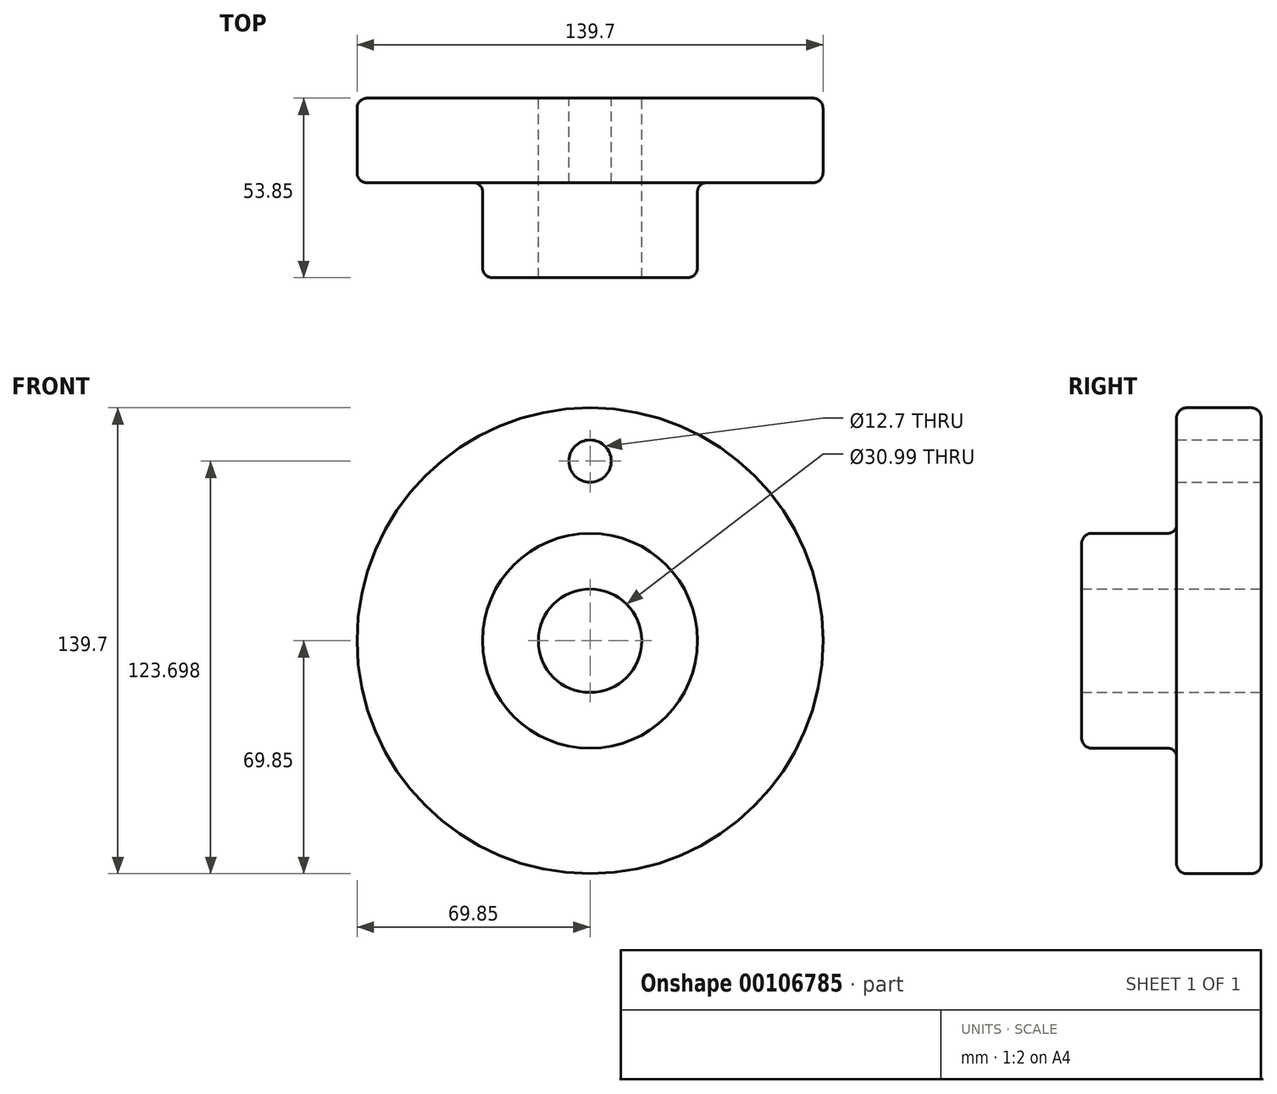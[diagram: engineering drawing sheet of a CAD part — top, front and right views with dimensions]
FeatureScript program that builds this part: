
annotation { "Feature Type Name" : "Feature", "Feature Type Description" : "" }
export const myFeature = defineFeature(function(context is Context, id is Id, definition is map)
    precondition{}
    {
        {
            var Q0;
            Q0=qCreatedBy(makeId("Front.planeOp"),FACE);
            var sketch = newSketch(context, id + "F0", { "sketchPlane" : qUnion([Q0])});
            skCircle(sketch, "E0", {"center": v(0, 0) * mm, "radius": 69.85 * mm});
            skSolve(sketch);
        }
        {
            var Q0;
            Q0 = qSketchRegion(id + "F0", true);
            extrude(context, id + "F1", {"entities" : qUnion([Q0]), "depth" : 25.4 * mm});
        }
        {
            var Q0;
            Q0=qCreatedBy(makeId("Front.planeOp"),FACE);
            var sketch = newSketch(context, id + "F2", { "sketchPlane" : qUnion([Q0])});
            skCircle(sketch, "E1", {"center": v(0, 0) * mm, "radius": 19.05 * mm});
            skCircle(sketch, "E2", {"center": v(0, 53.85) * mm, "radius": 6.35 * mm});
            skCircle(sketch, "E3", {"center": v(0, 0) * mm, "radius": 53.85 * mm, "construction": true});
            skSolve(sketch);
        }
        {
            var Q0;
            Q0 = qSketchRegion(id + "F2", true);
            extrude(context, id + "F3", {"entities" : qUnion([Q0]), "operationType" : NewBodyOperationType.REMOVE, "endBound" : BoundingType.THROUGH_ALL, "depth" : 25.4 * mm});
        }
        {
            var Q0;
            Q0=qCreatedBy(makeId("Right.planeOp"),FACE);
            var sketch = newSketch(context, id + "F4", { "sketchPlane" : qUnion([Q0])});
            skLineSegment(sketch, "E4", {"start": v(0, 0) * mm, "end": v(-45.3, 0) * mm, "construction": true});
            skLineSegment(sketch, "E5.bottom", {"start": v(0, 15.5) * mm, "end": v(-53.85, 15.5) * mm});
            skLineSegment(sketch, "E5.top", {"start": v(0, 32.23) * mm, "end": v(-50.8, 32.23) * mm});
            skLineSegment(sketch, "E5.left", {"start": v(0, 15.5) * mm, "end": v(0, 32.23) * mm});
            skLineSegment(sketch, "E5.right", {"start": v(-53.85, 15.5) * mm, "end": v(-53.85, 29.18) * mm});
            skPoint(sketch, "E6.visualSharp", {"position": v(-53.85, 32.23) * mm});
            skArc(sketch, "E6.filletArc", {"start": v(-50.8, 32.23) * mm, "mid": v(-52.96, 31.34) * mm, "end": v(-53.85, 29.18) * mm});
            skLineSegment(sketch, "E7.bottom", {"start": v(0, 32.23) * mm, "end": v(-25.3, 32.23) * mm});
            skLineSegment(sketch, "E7.top", {"start": v(0, 70) * mm, "end": v(-25.3, 70) * mm});
            skLineSegment(sketch, "E7.left", {"start": v(0, 32.23) * mm, "end": v(0, 70) * mm});
            skLineSegment(sketch, "E7.right", {"start": v(-25.3, 32.23) * mm, "end": v(-25.3, 70) * mm});
            skSolve(sketch);
        }
        {
            var Q0;
            Q0=makeQuery(id+"F4.imprint","IMPRINT",FACE,{"disambiguationData":[TD([[makeQuery(id+"F4.imprint","IMPRINT",EDGE,{"derivedFrom":sQuery(id+"F4.wireOp",EDGE,"E5.bottom")}),-1.0]])]});
            var Q1;
            Q1=sQuery(id+"F4.wireOp",EDGE,"E4");
            revolve(context, id + "F5", {"operationType" : NewBodyOperationType.ADD, "entities" : qUnion([Q0]), "axis" : qUnion([Q1]), "revolveType" : RevolveType.FULL});
        }
        {
            var Q0;
            Q0=makeQuery(id+"F1.opExtrude","CAP_EDGE",EDGE,{"disambiguationData":[OSD([sQuery(id+"F0.wireOp",EDGE,"E0")])],"isStart":false});
            fillet(context, id + "F6", {"entities" : qUnion([Q0]), "radius" : 3.05 * mm, "tangentPropagation" : true, "allowEdgeOverflow" : false});
        }
        {
            var Q0;
            Q0=makeQuery(id+"F1.opExtrude","CAP_EDGE",EDGE,{"disambiguationData":[OSD([sQuery(id+"F0.wireOp",EDGE,"E0")])],"isStart":true});
            fillet(context, id + "F7", {"entities" : qUnion([Q0]), "radius" : 3.05 * mm, "tangentPropagation" : true, "allowEdgeOverflow" : false});
        }
        {
            var Q0;
            Q0=makeQuery(id+"F5.boolean.opBoolean","INTERSECT",EDGE,{"derivedFrom":[makeQuery(id+"F1.opExtrude","CAP_FACE",FACE,{"disambiguationData":[OSD([sQuery(id+"F0.wireOp",EDGE,"E0")])],"isStart":false}),makeQuery(id+"F5.opRevolve","SWEPT_FACE",FACE,{"disambiguationData":[OSD([sQuery(id+"F4.wireOp",EDGE,"E5.top"),sQuery(id+"F4.wireOp",EDGE,"E7.bottom")])]})]});
            fillet(context, id + "F8", {"entities" : qUnion([Q0]), "radius" : 2.54 * mm, "tangentPropagation" : true, "allowEdgeOverflow" : false});
        }
    });
